# Revit family: NBS_DudleyIndustriesLimited_SoapDpnsrs_ModuloSlimlineBehindTheMirrorHandHygieneSystem2LTouchFreeSoapDispenser_92400BK
name_source: partatom
category: Specialty Equipment
units: mm (PartAtom-declared; Revit-internal decimal feet)

## family parameters
Always vertical = Yes
Cut with Voids When Loaded = No
Part Type = Normal
Room Calculation Point = No
Round Connector Dimension = Use Diameter
Shared = No
Work Plane-Based = No

## types (1)
- 92400BK Modulo Slimline 2L Soap Dispenser Battery Powered
    Accessories = Not required.,92405BK, Modulo Slimline Base Shelf, 600 mm.,92404BK,  Modulo Slimline Base Shelf, 1200 mm
    AssetType = Movable
    BIMObjectName = NBS_DudleyIndustriesLimited_SoapDispensers_ModuloSlimlineBehindTheMirrorHandHygieneSystem2LTouchFreeSoapDispenser_92400BK-BatteryPowered
    BlankingPlates = Not required.,Required
    Capacity = 2 L
    Category = Pr_40_70_22_81:Soap dispensers
    Color = Black
    Description = Soap dispenser
    Dimensions = 193 x 293 x 173 mm
    DispenserMaterial = NBS_DudleyIndustriesLimited_StainlessSteel_MatteBlackPowderCoated
    DurationUnit = year
    Finish = Powder-coated
    Form = Surface mounted
    FunnelMaterial = NBS_DudleyIndustriesLimited_Plastic_White
    IfcExportAs = IfcFurnitureType
    IfcExportType = NOTDEFINED
    ManufacturerName = Dudley Industries Limited
    ManufacturerURL = www.dudleyindustries.com
    Material = Stainless steel
    MaterialsBody = Stainless steel
    MaterialsFinishAndColour = Matte black, powder coated
    ModelReference = 92400BK Modulo Slimline 2L Soap Dispenser Battery Powered
    NBSCertification = www.nationalbimlibrary.com/cert/cpuq3ygh
    Name = SoapDispensers_ModuloSlimlineBehindTheMirrorHandHygieneSystem, 2LTouchFreeSoapDispenser_92400BK-BatteryPowered_DudleyIndustriesLimited
    NominalHeight = 293 mm
    NominalLength = 0 mm  [stored 0 ft]
    NominalWidth = 193 mm
    Operation = Automatic
    PlateMaterial = NBS_DudleyIndustriesLimited_StainlessSteel_MatteBlackPowderCoated
    ReservoirMaterial = NBS_DudleyIndustriesLimited_Plastic_Translucent
    Shape = Circle
    Uniclass2015Code = Pr_40_70_22_81
    Uniclass2015Title = Soap dispensers
    Uniclass2015Version = Products v1.22
    Version = 1
    WarrantyDescription = Ten year
    WarrantyDurationParts = Ten year
    WarrantyDurationUnit = year

note: [stored X ft] marks values corroborated as IEEE doubles in the binary element streams (Revit-internal decimal feet)

## geometry (parser evidence)
native form markers: Sweep x2
no freeform markers — native parametric forms only
